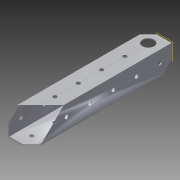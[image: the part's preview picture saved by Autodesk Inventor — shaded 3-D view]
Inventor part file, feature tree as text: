
AUTODESK INVENTOR PART (.ipt)
format: ipt  version: 2014 (Build 180170000, 170)  size: 1,167,872 bytes
history: native  units: in
note: dims shown in document units (in); Inventor stores cm internally (conversion verified against a paired STEP export)
features: pattern_circular x1, other x1, plane x1, extrude x1, imported_body x1, sketch x1
ambient origin geometry x8: Origin, YZ Plane, XZ Plane, XY Plane, X Axis, Y Axis, Z Axis, Center Point
bodies: Body1 (feature_tree)
feature tree (6):
  pattern_circular  "CirPattern2"
  other  "217-3426-STEP1"
  plane  "Work Plane1"
  extrude  "Extrusion1"  Depth=3937.0079in TaperAngle=0.0deg
  imported_body  "Base1"
  sketch  "Sketch1"  dims[d0=-7.0in d1=3937.0079in d2=0.0in]
